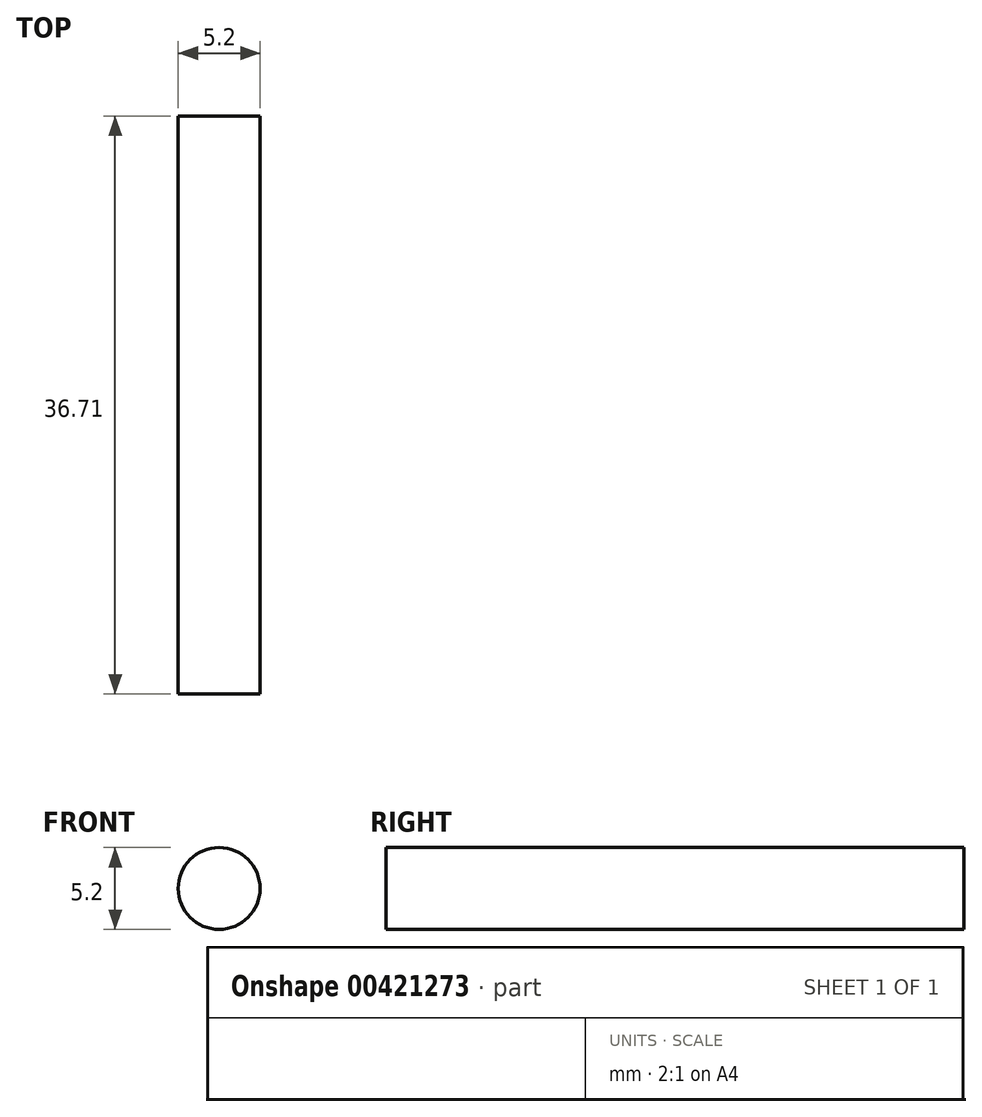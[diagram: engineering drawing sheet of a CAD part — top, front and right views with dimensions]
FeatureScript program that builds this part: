
annotation { "Feature Type Name" : "Feature", "Feature Type Description" : "" }
export const myFeature = defineFeature(function(context is Context, id is Id, definition is map)
    precondition{}
    {
        {
            var Q0;
            Q0=qCreatedBy(makeId("Front.planeOp"),FACE);
            var sketch = newSketch(context, id + "F0", { "sketchPlane" : qUnion([Q0])});
            skCircle(sketch, "E0", {"center": v(0, 0) * mm, "radius": 2.6 * mm});
            skSolve(sketch);
        }
        {
            var Q0;
            Q0=makeQuery(id+"F0.imprint","IMPRINT",FACE,{"disambiguationData":[TD([[makeQuery(id+"F0.imprint","IMPRINT",EDGE,{"derivedFrom":sQuery(id+"F0.wireOp",EDGE,"E0")}),1.0]])]});
            extrude(context, id + "F1", {"entities" : qUnion([Q0]), "depth" : 36.7 * mm, "offsetDistance" : 25 * mm});
        }
    });
